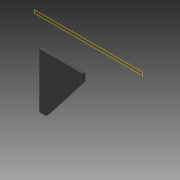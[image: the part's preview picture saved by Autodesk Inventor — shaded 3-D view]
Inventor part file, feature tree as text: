
AUTODESK INVENTOR PART (.ipt)
format: ipt  version: 2013 (Build 170138000, 138)  size: 109,056 bytes
history: native  units: in
note: dims shown in document units (in); Inventor stores cm internally (conversion verified against a paired STEP export)
features: sketch x4, other x3, hole x1, plane x1
ambient origin geometry x8: Origin, YZ Plane, XZ Plane, XY Plane, X Axis, Y Axis, Z Axis, Center Point
bodies: Solid1 (feature_tree)
feature tree (9):
  other  "side support.ipt"
  hole  "Hole1"  [1 undecoded]
  other  "Solid1::side support.ipt"
  other  "TaggingFeature1"
  sketch  "Sketch1"  dims[d0=0.3937in]
  sketch  "Sketch2"  dims[d2=9.8425in d3=0.4921in d4=0.0in d5=0.7874in d6=1.0827in d8=0.0in d9=0.134in d11=0.256in d12=0.118in]
  sketch  "Sketch3"  dims[d1=0.354in d7=0.75in d10=0.709in d13=0.224in d14=0.5635in d15=1.0in d16=0.8108in]
  plane  "Work Plane1"
  sketch  "Sketch4"
note: 1 required parameter value undecoded (feature->parameter linkage not recoverable at this tier; creation-order binding heuristic only, values carry confidence <= 0.55)
